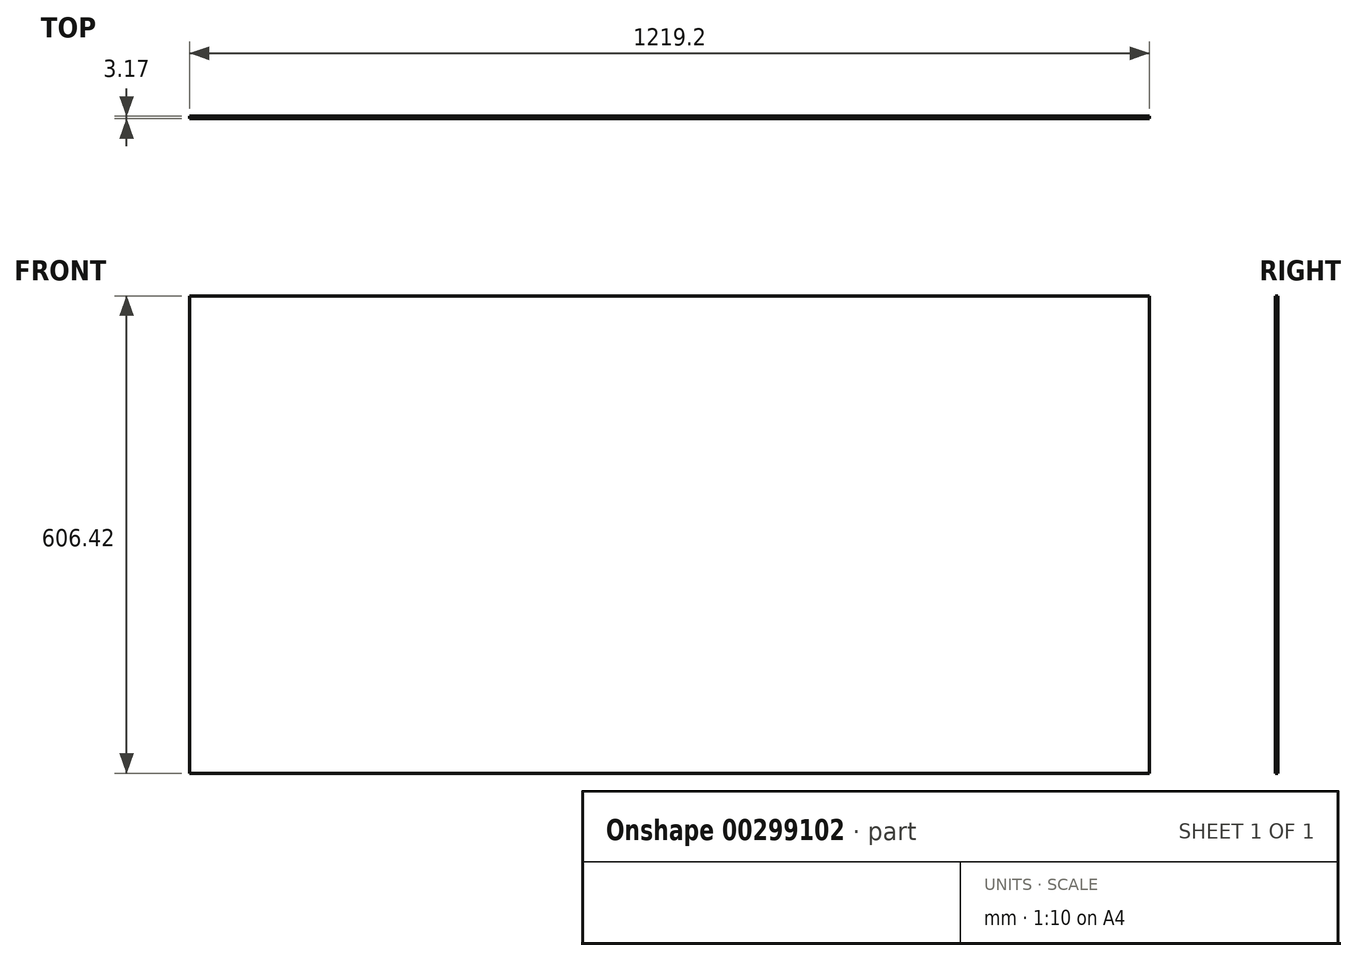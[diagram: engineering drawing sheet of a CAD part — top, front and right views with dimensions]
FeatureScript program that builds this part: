
annotation { "Feature Type Name" : "Feature", "Feature Type Description" : "" }
export const myFeature = defineFeature(function(context is Context, id is Id, definition is map)
    precondition{}
    {
        {
            var Q0;
            Q0=qCreatedBy(makeId("Front.planeOp"),FACE);
            var sketch = newSketch(context, id + "F0", { "sketchPlane" : qUnion([Q0])});
            skLineSegment(sketch, "E0.bottom", {"start": v(-609.6, 303.21) * mm, "end": v(609.6, 303.21) * mm});
            skLineSegment(sketch, "E0.top", {"start": v(-609.6, -303.21) * mm, "end": v(609.6, -303.21) * mm});
            skLineSegment(sketch, "E0.left", {"start": v(-609.6, 303.21) * mm, "end": v(-609.6, -303.21) * mm});
            skLineSegment(sketch, "E0.right", {"start": v(609.6, 303.21) * mm, "end": v(609.6, -303.21) * mm});
            skPoint(sketch, "E0.middle", {"position": v(0, 0) * mm});
            skSolve(sketch);
        }
        {
            var Q0;
            Q0 = qSketchRegion(id + "F0", true);
            extrude(context, id + "F1", {"entities" : qUnion([Q0]), "depth" : 3.17 * mm});
        }
    });
